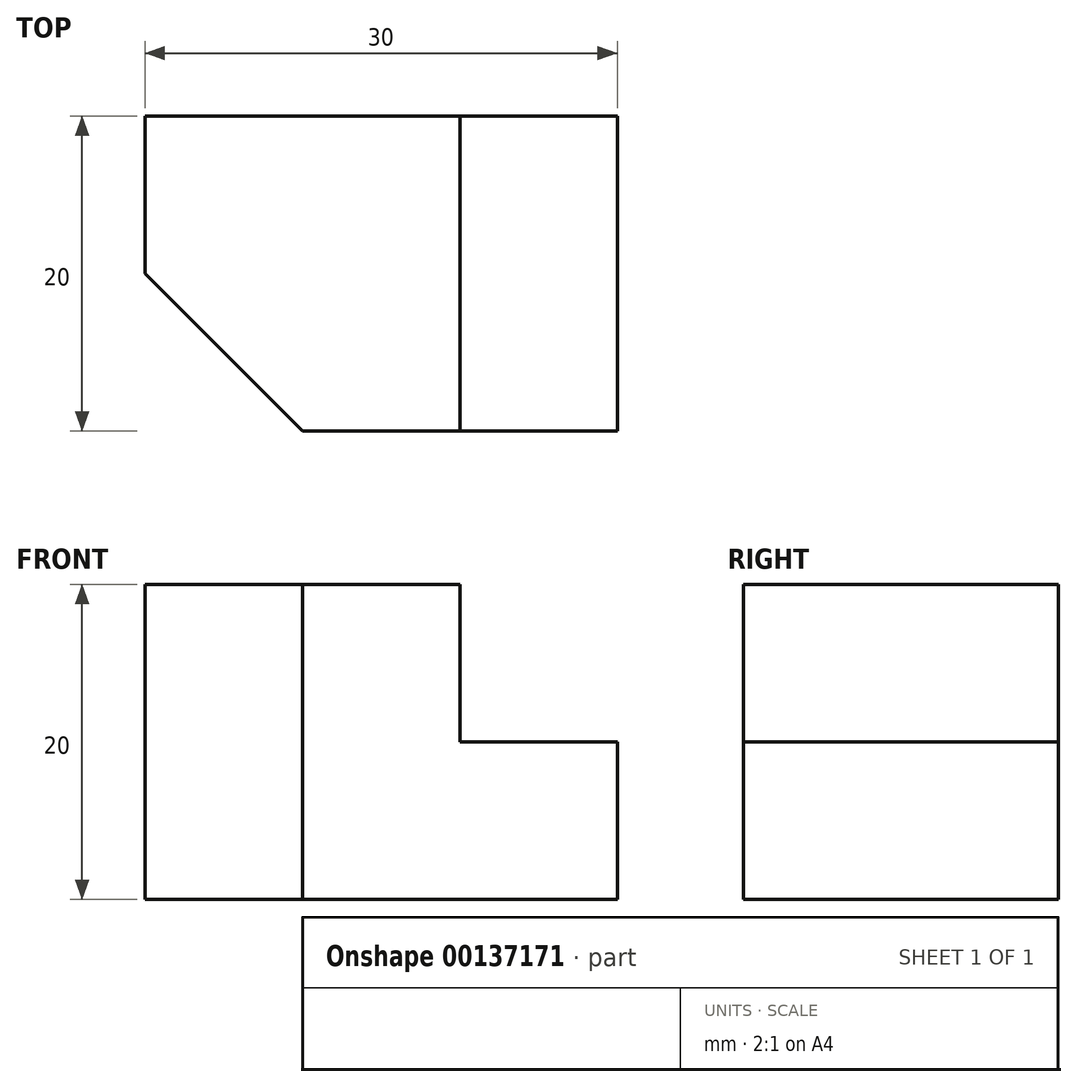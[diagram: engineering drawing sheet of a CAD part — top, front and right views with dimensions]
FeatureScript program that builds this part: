
annotation { "Feature Type Name" : "Feature", "Feature Type Description" : "" }
export const myFeature = defineFeature(function(context is Context, id is Id, definition is map)
    precondition{}
    {
        {
            var Q0;
            Q0=qCreatedBy(makeId("Front.planeOp"),FACE);
            var sketch = newSketch(context, id + "F0", { "sketchPlane" : qUnion([Q0])});
            skLineSegment(sketch, "E0.bottom", {"start": v(-26.2, 0) * mm, "end": v(3.8, 0) * mm});
            skLineSegment(sketch, "E0.top", {"start": v(-26.2, 20) * mm, "end": v(3.8, 20) * mm});
            skLineSegment(sketch, "E0.left", {"start": v(-26.2, 0) * mm, "end": v(-26.2, 20) * mm});
            skLineSegment(sketch, "E0.right", {"start": v(3.8, 0) * mm, "end": v(3.8, 20) * mm});
            skSolve(sketch);
        }
        {
            var Q0;
            Q0 = qSketchRegion(id + "F0", true);
            extrude(context, id + "F1", {"entities" : qUnion([Q0]), "depth" : 20 * mm});
        }
        {
            var Q0;
            Q0=qCreatedBy(makeId("Front.planeOp"),FACE);
            var sketch = newSketch(context, id + "F2", { "sketchPlane" : qUnion([Q0])});
            skLineSegment(sketch, "E1.0", {"start": v(-26.2, 20) * mm, "end": v(3.8, 20) * mm});
            skLineSegment(sketch, "E1.1", {"start": v(3.8, 0) * mm, "end": v(3.8, 20) * mm});
            skLineSegment(sketch, "E2", {"start": v(-6.2, 20) * mm, "end": v(-6.2, 10) * mm});
            skLineSegment(sketch, "E3", {"start": v(-6.2, 10) * mm, "end": v(3.8, 10) * mm});
            skSolve(sketch);
        }
        {
            var Q0;
            Q0 = qSketchRegion(id + "F2", true);
            extrude(context, id + "F3", {"entities" : qUnion([Q0]), "operationType" : NewBodyOperationType.REMOVE, "depth" : 30 * mm});
        }
        {
            var Q0;
            Q0=qCreatedBy(makeId("Top.planeOp"),FACE);
            var sketch = newSketch(context, id + "F4", { "sketchPlane" : qUnion([Q0])});
            skLineSegment(sketch, "E4.0", {"start": v(-26.2, -20) * mm, "end": v(-26.2, 0) * mm});
            skLineSegment(sketch, "E4.1", {"start": v(-26.2, -20) * mm, "end": v(-6.2, -20) * mm});
            skLineSegment(sketch, "E5", {"start": v(-26.2, -10) * mm, "end": v(-16.2, -20) * mm});
            skSolve(sketch);
        }
        {
            var Q0;
            Q0 = qSketchRegion(id + "F4", true);
            extrude(context, id + "F5", {"entities" : qUnion([Q0]), "operationType" : NewBodyOperationType.REMOVE, "endBound" : BoundingType.SYMMETRIC, "depth" : 50 * mm});
        }
    });
